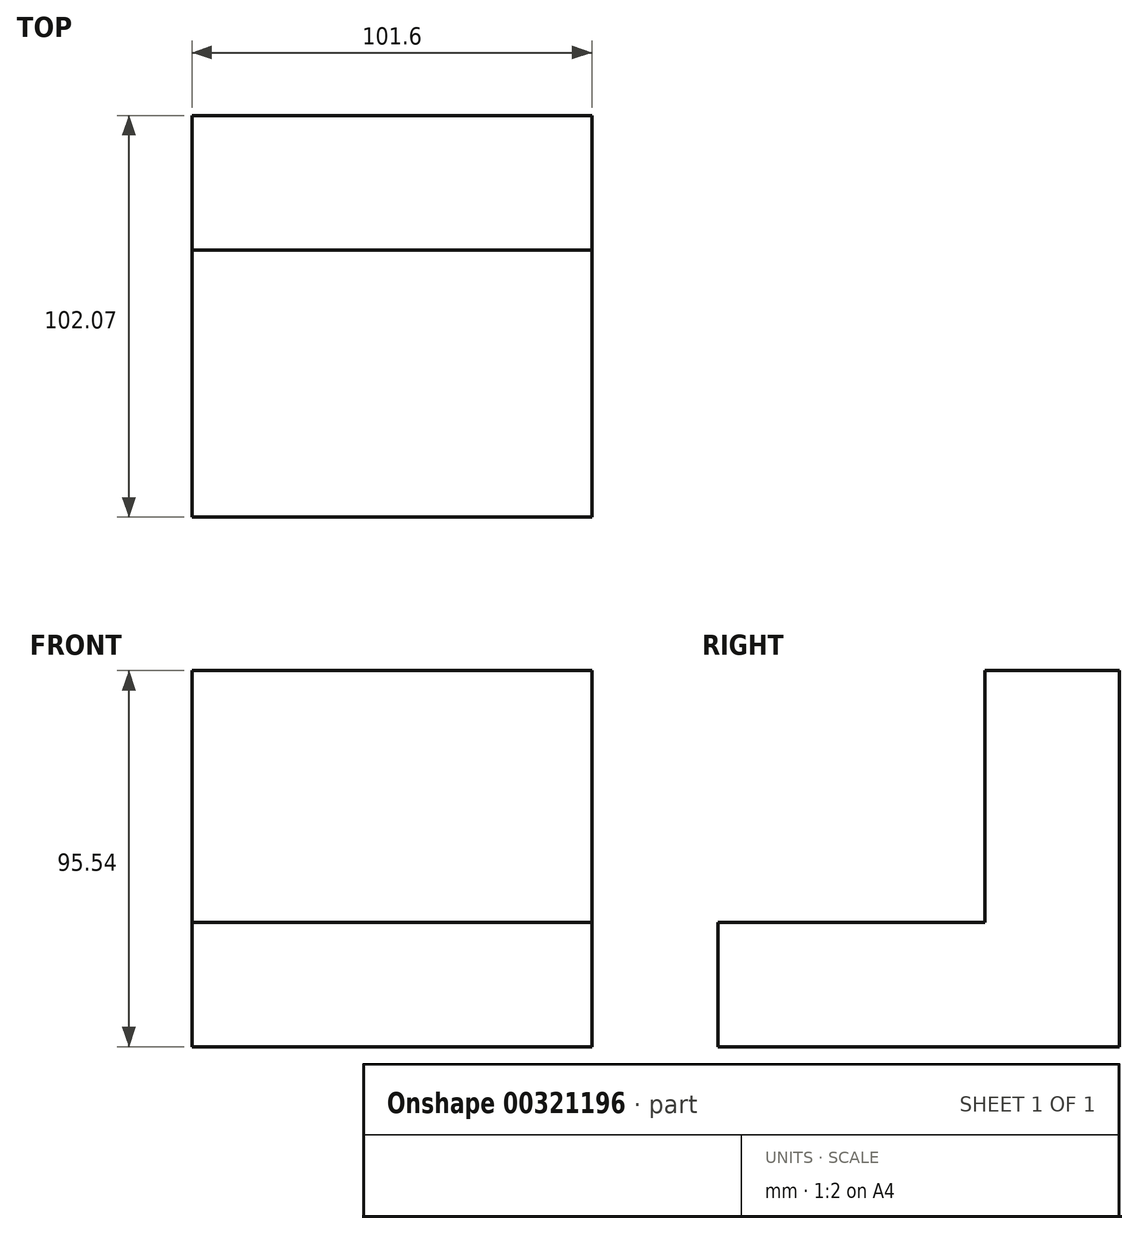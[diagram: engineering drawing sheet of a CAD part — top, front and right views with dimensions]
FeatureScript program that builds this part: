
annotation { "Feature Type Name" : "Feature", "Feature Type Description" : "" }
export const myFeature = defineFeature(function(context is Context, id is Id, definition is map)
    precondition{}
    {
        {
            var Q0;
            Q0=qCreatedBy(makeId("Right.planeOp"),FACE);
            var sketch = newSketch(context, id + "F0", { "sketchPlane" : qUnion([Q0])});
            skLineSegment(sketch, "E0", {"start": v(-52.87, -34.32) * mm, "end": v(49.2, -34.32) * mm});
            skLineSegment(sketch, "E1", {"start": v(49.2, -34.32) * mm, "end": v(49.2, 61.22) * mm});
            skLineSegment(sketch, "E2", {"start": v(49.2, 61.22) * mm, "end": v(15, 61.22) * mm});
            skLineSegment(sketch, "E3", {"start": v(15, 61.22) * mm, "end": v(15, -2.74) * mm});
            skLineSegment(sketch, "E4", {"start": v(15, -2.74) * mm, "end": v(-52.87, -2.74) * mm});
            skLineSegment(sketch, "E5", {"start": v(-52.87, -2.74) * mm, "end": v(-52.87, -34.32) * mm});
            skSolve(sketch);
        }
        {
            var Q0;
            Q0=makeQuery(id+"F0.imprint","IMPRINT",FACE,{"disambiguationData":[TD([[makeQuery(id+"F0.imprint","IMPRINT",EDGE,{"derivedFrom":sQuery(id+"F0.wireOp",EDGE,"E0")}),1.0]])]});
            extrude(context, id + "F1", {"entities" : qUnion([Q0]), "depth" : 101.6 * mm});
        }
    });
